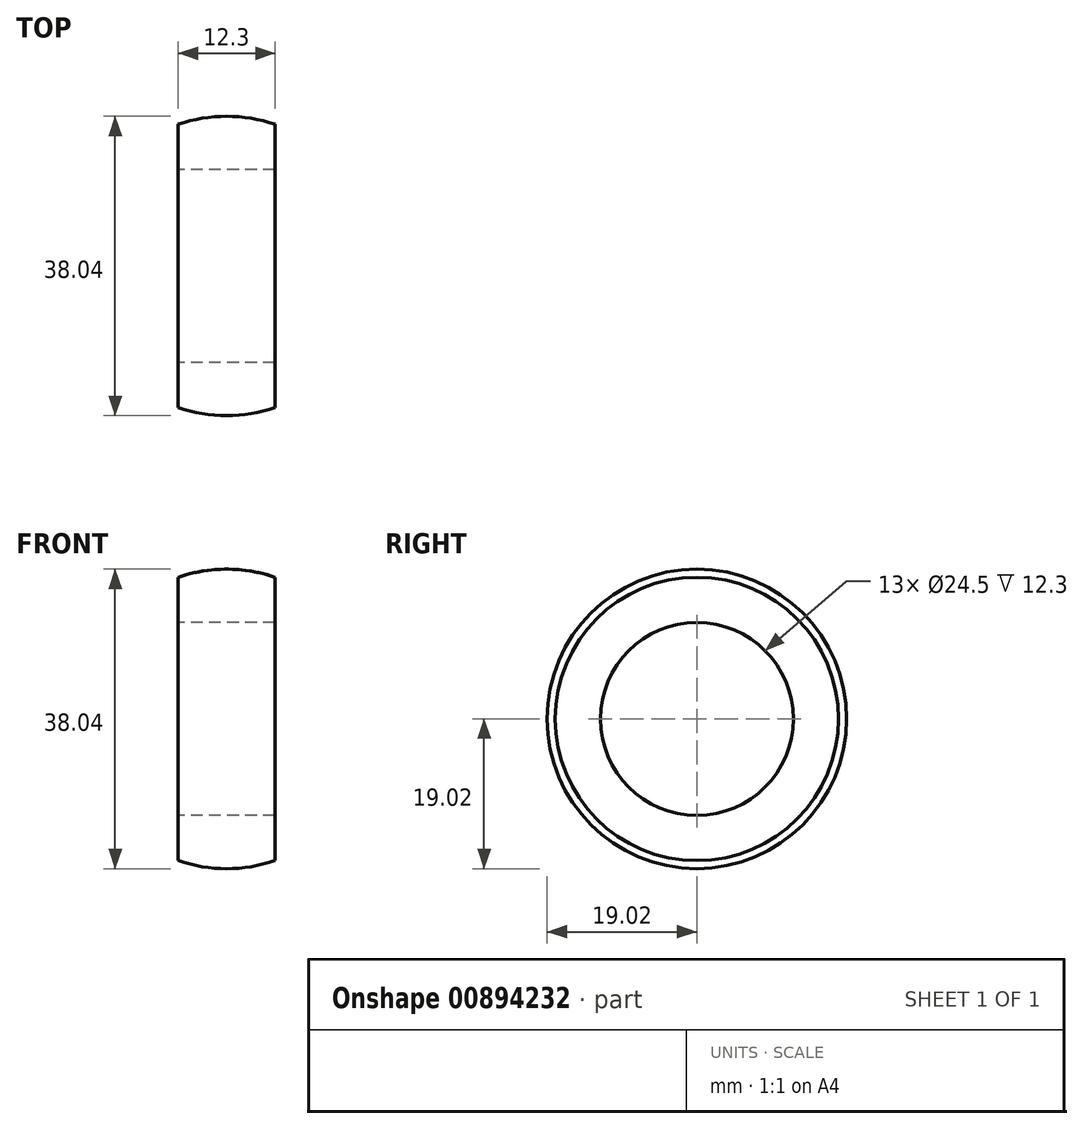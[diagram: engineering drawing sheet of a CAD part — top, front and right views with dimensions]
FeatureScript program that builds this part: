
annotation { "Feature Type Name" : "Feature", "Feature Type Description" : "" }
export const myFeature = defineFeature(function(context is Context, id is Id, definition is map)
    precondition{}
    {
        {
            var Q0;
            Q0=qCreatedBy(makeId("Front.planeOp"),FACE);
            var sketch = newSketch(context, id + "F0", { "sketchPlane" : qUnion([Q0])});
            skLineSegment(sketch, "E0", {"start": v(0, 12.25) * mm, "end": v(12.3, 12.25) * mm});
            skLineSegment(sketch, "E1", {"start": v(12.3, 12.25) * mm, "end": v(12.3, 18) * mm});
            skLineSegment(sketch, "E2", {"start": v(0, 12.25) * mm, "end": v(0, 18) * mm});
            skArc(sketch, "E3", {"start": v(12.3, 18) * mm, "mid": v(6.15, 19.02) * mm, "end": v(0, 18) * mm});
            skLineSegment(sketch, "E4", {"start": v(0, 0) * mm, "end": v(12.3, 0) * mm, "construction": true});
            skSolve(sketch);
        }
        {
            var Q0;
            Q0=makeQuery(id+"F0.imprint","IMPRINT",FACE,{"disambiguationData":[TD([[makeQuery(id+"F0.imprint","IMPRINT",EDGE,{"derivedFrom":sQuery(id+"F0.wireOp",EDGE,"E0")}),1.0]])]});
            var Q1;
            Q1=qConstructionFilter(qBodyType(qCreatedBy(id+"F0",EDGE),BodyType.WIRE),ConstructionObject.NO);
            var Q2;
            Q2=sQuery(id+"F0.wireOp",EDGE,"E4");
            revolve(context, id + "F1", {"surfaceOperationType" : NewSurfaceOperationType.NEW, "entities" : qUnion([Q0]), "surfaceEntities" : qUnion([Q1]), "axis" : qUnion([Q2]), "revolveType" : RevolveType.FULL});
        }
    });
